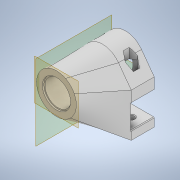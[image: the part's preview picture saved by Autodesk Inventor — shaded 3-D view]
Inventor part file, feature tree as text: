
AUTODESK INVENTOR PART (.ipt)
format: ipt  version: 2020 (Build 240168000, 168)  size: 365,056 bytes
history: native  units: in
note: dims shown in document units (in); Inventor stores cm internally (conversion verified against a paired STEP export)
features: sketch x10, extrude x8, projected_geometry x4, plane x3, chamfer x2, loft x1
ambient origin geometry x8: Origin, YZ Plane, XZ Plane, XY Plane, X Axis, Y Axis, Z Axis, Center Point
bodies: Solid1 (feature_tree)
feature tree (28):
  extrude  "Extrusion1"  Depth=1.25in
  sketch  "Sketch2"  dims[d2=3.0in d3=1.0157in]
  plane  "Work Plane1"
  loft  "Loft1"
  plane  "Work Plane2"
  extrude  "Extrusion4"  Depth=1.5in
  extrude  "Extrusion5"  Depth=0.375in
  extrude  "Extrusion6"  Depth=1.0in
  plane  "Work Plane3"
  extrude  "Extrusion7"  TaperAngle=0.0deg  [1 undecoded]
  extrude  "Extrusion8"  Depth=0.5in
  extrude  "Extrusion10"  Depth=0.75in
  extrude  "Extrusion11"  Depth=1.0in TaperAngle=0.0deg
  chamfer  "Chamfer1"  Distance=1.891in
  chamfer  "Chamfer2"  Distance=1.126in
  sketch  "Sketch1"  dims[d0=1.25in d1=1.226in]
  projected_geometry  "Projected Loop1"
  projected_geometry  "Projected Loop2"
  sketch  "Sketch3"  dims[d4=0.5079in d5=1.5in]
  sketch  "Sketch7"  dims[d6=0.25in d7=0.375in]
  projected_geometry  "Projected Loop3"
  sketch  "Sketch8"  dims[d8=1.0in d9=0.0in d10=2.0in]
  sketch  "Sketch9"  dims[d11=0.0in d12=90.0deg d13=0.0in d14=90.0deg]
  sketch  "Sketch10"  dims[d28=-0.5in d34=0.5in]
  projected_geometry  "Projected Loop4"
  sketch  "Sketch11"  dims[d35=0.75in d36=0.2656in]
  sketch  "Sketch13"  dims[d37=0.7874in d39=1.5in d40=0.3937in d42=1.0in d44=1.891in d45=0.0in]
  sketch  "Sketch15"  dims[d46=0.4532in d47=1.891in d48=0.0in d49=1.126in d50=0.0in d51=0.0in d52=2.5in d53=1.25in d54=0.5in d55=0.5in d56=1.5in d57=0.0in d58=45.0deg d59=45.0deg d60=1.0in d61=0.5in d62=0.0in d66=1.226in d67=0.065in d68=0.0in d69=1.226in d70=0.065in d71=0.0in d72=0.05in d73=0.125in d74=45.0deg d75=0.03in d76=0.125in d77=45.0deg]
note: 1 required parameter value undecoded (feature->parameter linkage not recoverable at this tier; creation-order binding heuristic only, values carry confidence <= 0.55)
